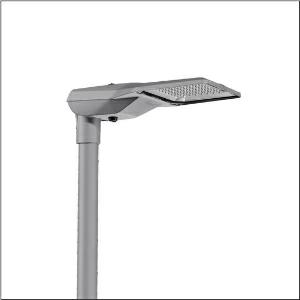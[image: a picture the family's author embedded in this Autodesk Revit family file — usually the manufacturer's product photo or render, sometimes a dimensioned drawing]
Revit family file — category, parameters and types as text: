
# Revit family: streetlight_sl_21_iq_midi___st1_0ab_5xe3m31y08mb_ceed
name_source: partatom
category: Lighting Fixtures
units: mm (PartAtom-declared; Revit-internal decimal feet)

## family parameters
Cut with Voids When Loaded = No
Host = Face
Light Source = No
Part Type = Normal
Room Calculation Point = No
Round Connector Dimension = Use Diameter
Shared = No

## types (1)
- --- (1 x LED, 16140 lm, 129.3 W, 3000K)
    Apparent Load = 129 VA
    CIE Flux Codes = 38 73 97 100 100
    Color Rendering = 70
    Color Temperature = 3000K
    Default Elevation = 1800 mm
    Description = Streetlight SL 21 iQ midi, mast luminaire, primary light control with lens, of PMMA, primary optical cover: cover, of toughened safety glass, transparent, light distribution: ST1.0aB, light emission: direct distribution, primary light characteristic: asymmetric, installation type: post-top, side-entry, LED, High Power LED, rated luminous flux: 16.140lm, luminous efficacy: 125lm/W, light colour: 730, colour temperature: 3000K, control: presetting dimming logarithmic, Street-Remote, Auto-Match, Temp-Guard, Lumen-Switch, Night-Set, Smart-Wire, Light-Fading, Desk-Remote (wireless, voltage-free reading and setting of iQ features in the workshop via application-optimized NFC function/RFID function), optimised constant luminous flux control (CLO 2.0), mains connection: 230..240V, AC, 50/60Hz, start of lifetime: 129W, end of service life: 142W, reduction: 56W, luminaire housing, of diecast aluminium, powder-coated, Siteco® metallic grey (DB 702S), corrosivity category C5 mid according to DIN EN ISO 12944, please order mast flange separately, inclination adjustable: 0°, 5°, 10°, 15°, sealing non-destructively replaceable, multi-level sealing system, length: 644mm, width: 335mm, height: 110mm, mast flange for spigot size: 42mm (side-entry): 5XC10008XM4, 60/48mm (side-entry/post-top): 5XC10108XM2, 76/60mm (side-entry/post-top): 5XC10108XM1, Smart Interface below and above, protection rating (complete): IP66, insulation class (complete): insulation class II (safety insulation), certification: CE, ENEC, ENEC+, VDE, impact resistance: IK09, permissible operating ambient temperature for outdoor applications: -40..+50°C, standard-compliant lighting for roads and squares, packaging unit: 1 piece

Light Distribution: ST1.0aB
    Height = 111 mm
    Lamp = 1 x LED
    Lamp Light Flux = 16140 lm
    Lamp Power = 129.3 W
    Lamp count = 1
    Length = 644 mm
    Luminous efficacy = 125 lm/W
    Manufacturer = Siteco
    ModVariant = No
    Model = 5XE3M31Y08MB
    Number of Poles = 1
    OnlyDefault = Yes
    Power Factor = 1
    Product Name = Streetlight SL 21 iQ midi | ST1.0aB
    Product group = mast luminaire | pylon top
    ProductGroupID = 6100
    Protection Class = Protection class II
    Protection Degree = IP 66
    RLX_Detail_Level = 1
    RLX_Emergency_Light_Flux = 0 lm
    RLX_Emergency_Type = 0
    RLX_Emergency_Type_DB = No
    RlxData = <blob elided: 90845 chars, md5=df92c893>
    Socket = socket
    Standby Power = 0 W
    System Light Flux = 16141 lm
    System Power = 129 W
    Type Comments = factory setting: luminous flux: 100 % | dim-lin: 254 | 672 mA
    Type Image = l_1004304.jpg
    URL = http://relux.com
    VarID = @adj_042369
    Voltage = 0 V
    Weight = 0.00 kg
    Width = 336 mm

## geometry (parser evidence)
native form markers: Blend x4, Sweep x10
no freeform markers — native parametric forms only
